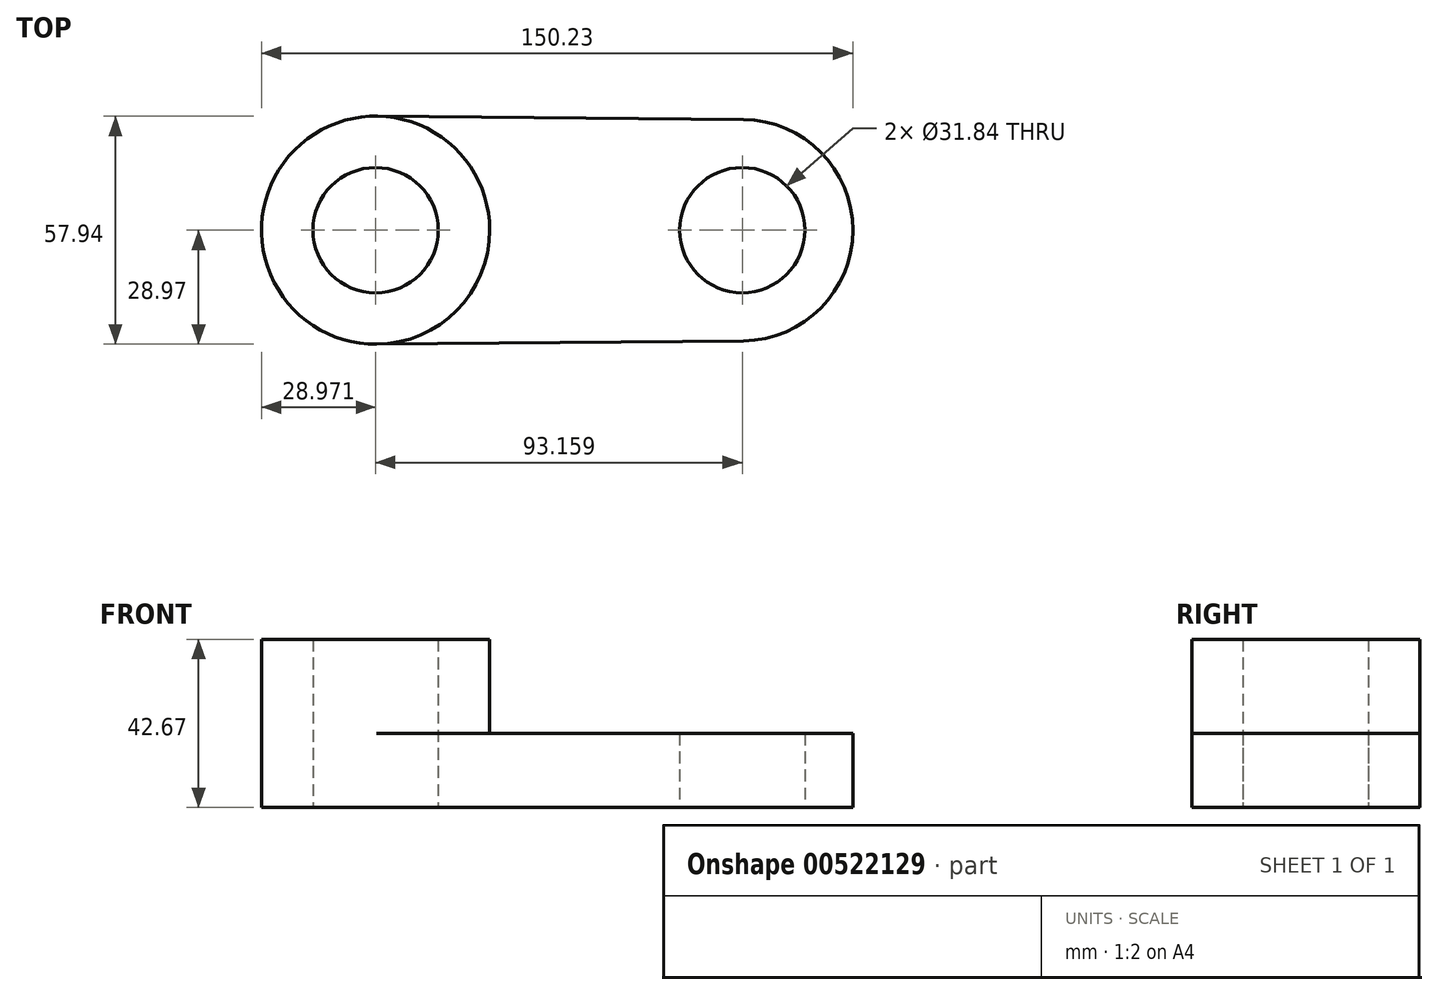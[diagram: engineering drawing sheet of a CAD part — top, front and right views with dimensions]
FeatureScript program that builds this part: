
annotation { "Feature Type Name" : "Feature", "Feature Type Description" : "" }
export const myFeature = defineFeature(function(context is Context, id is Id, definition is map)
    precondition{}
    {
        {
            var Q0;
            Q0=qCreatedBy(makeId("Top.planeOp"),FACE);
            var sketch = newSketch(context, id + "F0", { "sketchPlane" : qUnion([Q0])});
            skCircle(sketch, "E0", {"center": v(-46.58, 0) * mm, "radius": 15.92 * mm});
            skCircle(sketch, "E1", {"center": v(46.58, 0) * mm, "radius": 15.92 * mm});
            skArc(sketch, "E2", {"start": v(-46.3, 28.97) * mm, "mid": v(-75.55, 0) * mm, "end": v(-46.3, -28.97) * mm});
            skArc(sketch, "E3", {"start": v(46.84, -28.1) * mm, "mid": v(74.68, 0) * mm, "end": v(46.84, 28.1) * mm});
            skLineSegment(sketch, "E4", {"start": v(-46.3, 28.97) * mm, "end": v(46.84, 28.1) * mm});
            skLineSegment(sketch, "E5", {"start": v(46.84, -28.1) * mm, "end": v(-46.3, -28.97) * mm});
            skArc(sketch, "E6", {"start": v(-46.3, -28.97) * mm, "mid": v(-17.6, 0) * mm, "end": v(-46.3, 28.97) * mm});
            skSolve(sketch);
        }
        {
            var Q0;
            Q0=makeQuery(id+"F0.imprint","IMPRINT",FACE,{"disambiguationData":[TD([[makeQuery(id+"F0.imprint","IMPRINT",EDGE,{"derivedFrom":sQuery(id+"F0.wireOp",EDGE,"E1")}),-1.0]])]});
            extrude(context, id + "F1", {"entities" : qUnion([Q0]), "depth" : 18.8 * mm, "offsetDistance" : 25.4 * mm});
        }
        {
            var Q0;
            Q0=makeQuery(id+"F0.imprint","IMPRINT",FACE,{"disambiguationData":[TD([[makeQuery(id+"F0.imprint","IMPRINT",EDGE,{"derivedFrom":sQuery(id+"F0.wireOp",EDGE,"E0")}),-1.0]])]});
            extrude(context, id + "F2", {"entities" : qUnion([Q0]), "operationType" : NewBodyOperationType.ADD, "depth" : 42.67 * mm, "offsetDistance" : 25.4 * mm});
        }
    });
